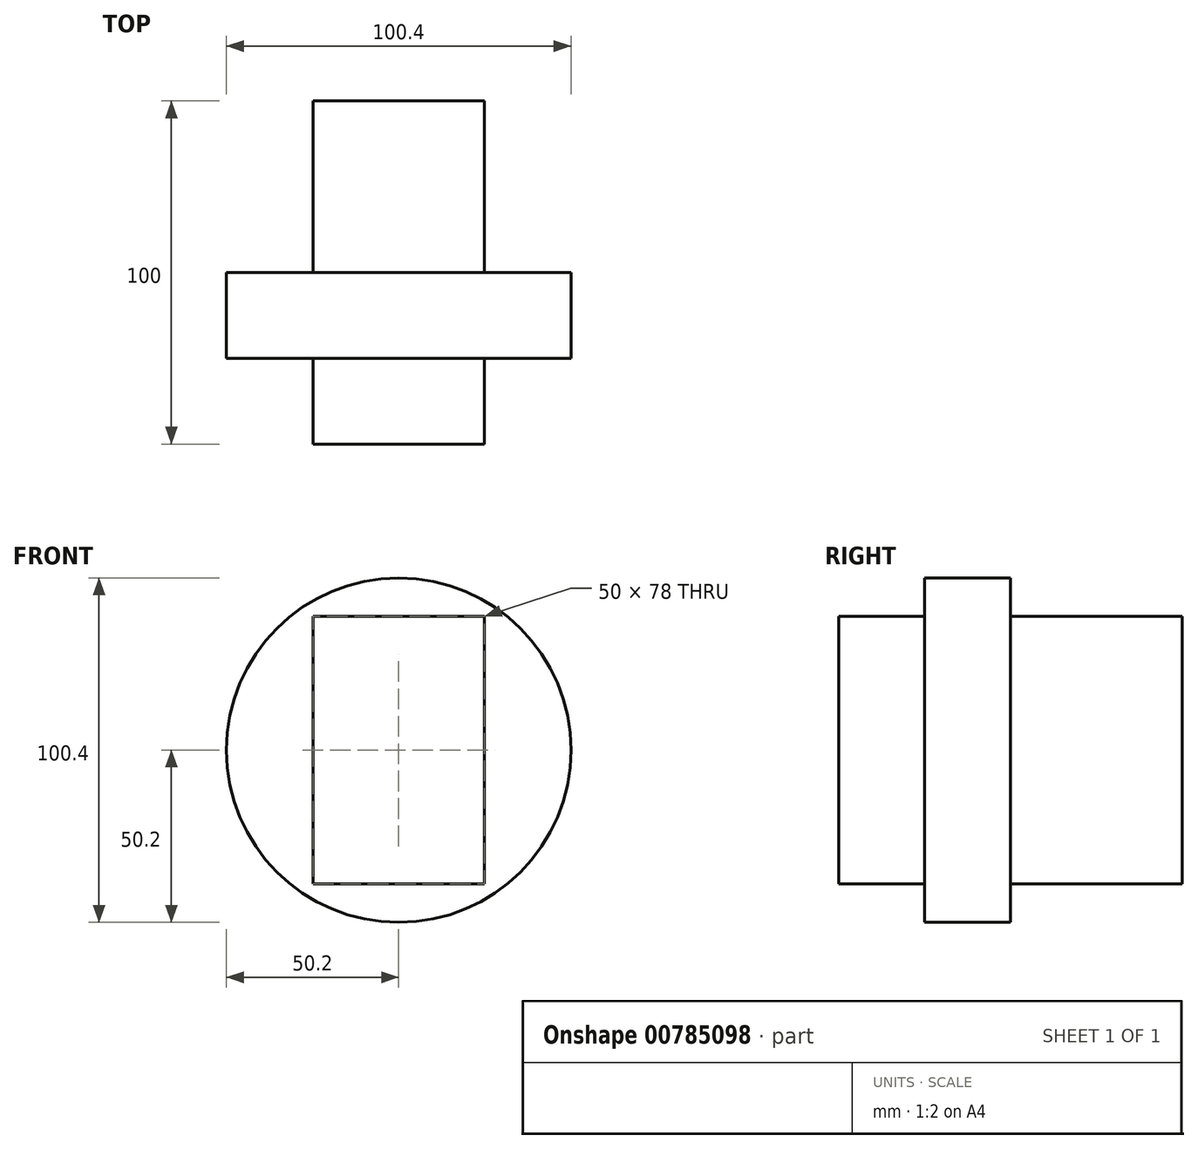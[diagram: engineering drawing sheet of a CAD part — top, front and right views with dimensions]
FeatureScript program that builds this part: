
annotation { "Feature Type Name" : "Feature", "Feature Type Description" : "" }
export const myFeature = defineFeature(function(context is Context, id is Id, definition is map)
    precondition{}
    {
        {
            var Q0;
            Q0=qCreatedBy(makeId("Top.planeOp"),FACE);
            var sketch = newSketch(context, id + "F0", { "sketchPlane" : qUnion([Q0])});
            skLineSegment(sketch, "E0.bottom", {"start": v(25, -50) * mm, "end": v(-25, -50) * mm});
            skLineSegment(sketch, "E0.top", {"start": v(25, 50) * mm, "end": v(-25, 50) * mm});
            skLineSegment(sketch, "E0.left", {"start": v(25, -50) * mm, "end": v(25, 50) * mm});
            skLineSegment(sketch, "E0.right", {"start": v(-25, -50) * mm, "end": v(-25, 50) * mm});
            skPoint(sketch, "E0.middle", {"position": v(0, 0) * mm});
            skSolve(sketch);
        }
        {
            var Q0;
            Q0 = qSketchRegion(id + "F0", true);
            extrude(context, id + "F1", {"entities" : qUnion([Q0]), "endBound" : BoundingType.SYMMETRIC, "depth" : 78 * mm, "offsetDistance" : 25 * mm});
        }
        {
            var Q0;
            Q0=qCreatedBy(makeId("Front.planeOp"),FACE);
            var sketch = newSketch(context, id + "F2", { "sketchPlane" : qUnion([Q0])});
            skCircle(sketch, "E1", {"center": v(0, 0) * mm, "radius": 50.2 * mm});
            skSolve(sketch);
        }
        {
            var Q0;
            Q0 = qSketchRegion(id + "F2", true);
            extrude(context, id + "F3", {"entities" : qUnion([Q0]), "operationType" : NewBodyOperationType.ADD, "depth" : 25 * mm, "offsetDistance" : 25 * mm});
        }
    });
